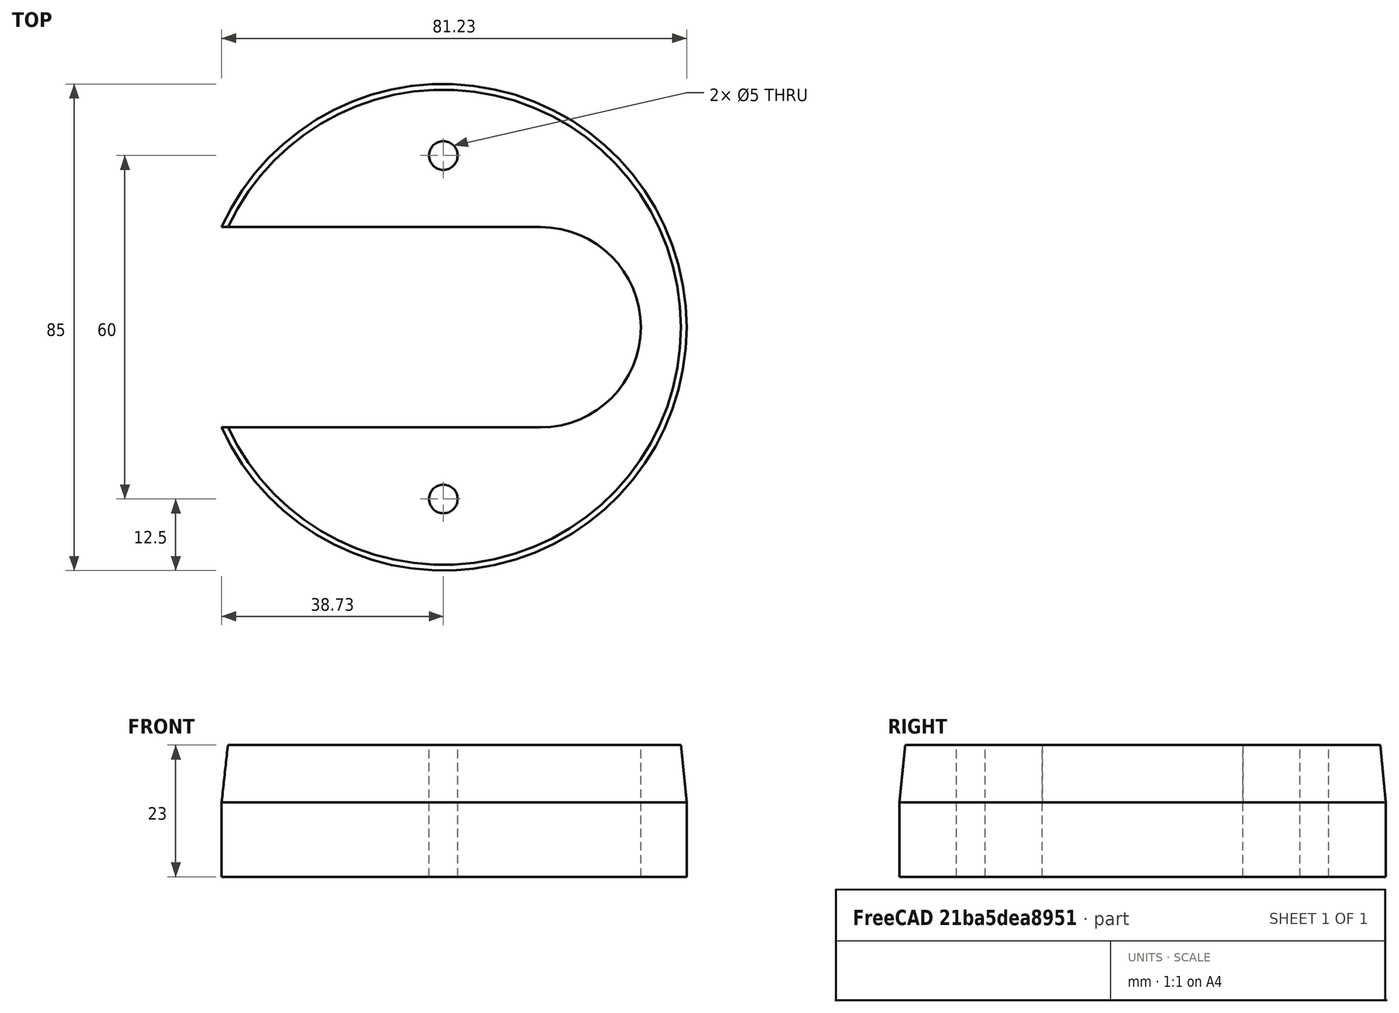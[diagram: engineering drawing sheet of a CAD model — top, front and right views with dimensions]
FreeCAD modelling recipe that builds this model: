
FCSTD DOCUMENT  (FreeCAD 0.19R24291 (Git))
Label: cup_lifter
License: All rights reserved
LicenseURL: http://en.wikipedia.org/wiki/All_rights_reserved
objects: Part::Cylinder×4, Part::Cut×4, Part::Box×1, Part::Chamfer×1
note: 10 computed .brp shape members not serialized (recipe doc carries the construction recipe); baked Part::Feature solids carry a one-line shape summary decoded from their .brp

FEATURE [Part::Cylinder] Cylinder
  Angle = 360
  AttacherType = Attacher::AttachEngine3D
  Height = 23
  Radius = 42.5
FEATURE [Part::Cylinder] Cylinder001
  Angle = 360
  AttacherType = Attacher::AttachEngine3D
  Height = 23
  Placement = pos=(17,0,0) rot=(0,0,1;0rad)
  Radius = 17.5
FEATURE [Part::Box] Box  label="Cube"
  AttacherType = Attacher::AttachEngine3D
  Height = 23
  Length = 59.5
  Placement = pos=(-42.5,-17.5,0) rot=(0,0,1;0rad)
  Width = 35
FEATURE [Part::Cylinder] Cylinder002
  Angle = 360
  AttacherType = Attacher::AttachEngine3D
  Height = 23
  Placement = pos=(0,30,0) rot=(0,0,1;0rad)
  Radius = 2.5
FEATURE [Part::Cylinder] Cylinder003
  Angle = 360
  AttacherType = Attacher::AttachEngine3D
  Height = 23
  Placement = pos=(0,-30,0) rot=(0,0,1;0rad)
  Radius = 2.5
FEATURE [Part::Chamfer] Chamfer
  Base = -> Cylinder
  Edges = 1 edges: [Edge1 r1=10 r2=1]
FEATURE [Part::Cut] Cut
  Base = -> Chamfer
  Tool = -> Cylinder001
FEATURE [Part::Cut] Cut001
  Base = -> Cut
  Tool = -> Box
FEATURE [Part::Cut] Cut002
  Base = -> Cut001
  Tool = -> Cylinder002
FEATURE [Part::Cut] Cut003
  Base = -> Cut002
  Tool = -> Cylinder003
